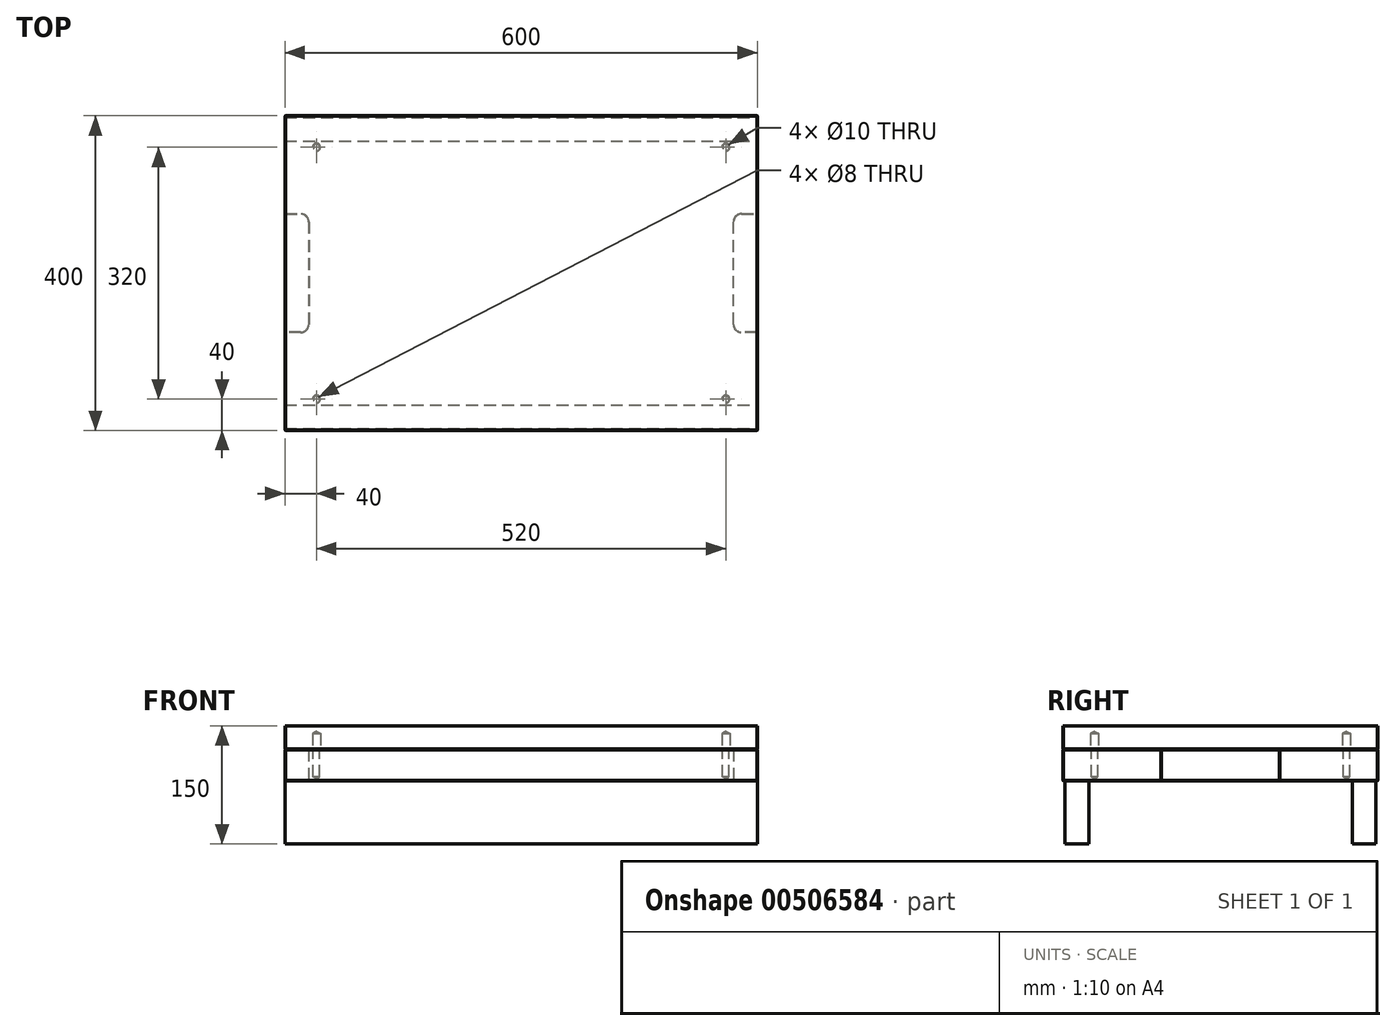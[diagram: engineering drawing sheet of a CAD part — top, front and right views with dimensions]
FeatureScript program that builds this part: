
annotation { "Feature Type Name" : "Feature", "Feature Type Description" : "" }
export const myFeature = defineFeature(function(context is Context, id is Id, definition is map)
    precondition{}
    {
        {
            assignVariable(context, id + "F0", {"name" : "Altezza_Sotto", "anyValue" : 40});
        }
        {
            assignVariable(context, id + "F1", {"name" : "Altezza_Sopra", "anyValue" : 30});
        }
        {
            var Q0;
            Q0=qCreatedBy(makeId("Top.planeOp"),FACE);
            var sketch = newSketch(context, id + "F2", { "sketchPlane" : qUnion([Q0])});
            skLineSegment(sketch, "E0", {"start": v(-250, 0) * mm, "end": v(350, 0) * mm, "construction": true});
            skLineSegment(sketch, "E1.bottom", {"start": v(350, 75) * mm, "end": v(330, 75) * mm});
            skLineSegment(sketch, "E1.top", {"start": v(350, -75) * mm, "end": v(330, -75) * mm});
            skLineSegment(sketch, "E1.left", {"start": v(350, 75) * mm, "end": v(350, -75) * mm});
            skLineSegment(sketch, "E1.right", {"start": v(320, 65) * mm, "end": v(320, -65) * mm});
            skPoint(sketch, "E2.visualSharp", {"position": v(320, -75) * mm});
            skArc(sketch, "E2.filletArc", {"start": v(320, -65) * mm, "mid": v(322.93, -72.07) * mm, "end": v(330, -75) * mm});
            skPoint(sketch, "E3.visualSharp", {"position": v(320, 75) * mm});
            skArc(sketch, "E3.filletArc", {"start": v(330, 75) * mm, "mid": v(322.93, 72.07) * mm, "end": v(320, 65) * mm});
            skLineSegment(sketch, "E4", {"start": v(50, 200) * mm, "end": v(50, -200) * mm, "construction": true});
            skLineSegment(sketch, "E5.MirrorCS", {"start": v(-250, 75) * mm, "end": v(-230, 75) * mm});
            skLineSegment(sketch, "E6.MirrorCS", {"start": v(-220, 65) * mm, "end": v(-220, -65) * mm});
            skArc(sketch, "E7.MirrorCS", {"start": v(-220, -65) * mm, "mid": v(-222.93, -72.07) * mm, "end": v(-230, -75) * mm});
            skArc(sketch, "E8.MirrorCS", {"start": v(-230, 75) * mm, "mid": v(-222.93, 72.07) * mm, "end": v(-220, 65) * mm});
            skLineSegment(sketch, "E9.MirrorCS", {"start": v(-250, -75) * mm, "end": v(-230, -75) * mm});
            skPoint(sketch, "E10", {"position": v(-210, 160) * mm});
            skPoint(sketch, "E11", {"position": v(310, 160) * mm});
            skPoint(sketch, "E12", {"position": v(310, -160) * mm});
            skPoint(sketch, "E13", {"position": v(-210, -160) * mm});
            skLineSegment(sketch, "E14", {"start": v(-220, 0) * mm, "end": v(-250, 0) * mm});
            skLineSegment(sketch, "E15.bottom", {"start": v(350, 200) * mm, "end": v(-250, 200) * mm});
            skLineSegment(sketch, "E15.top", {"start": v(350, -200) * mm, "end": v(-250, -200) * mm});
            skLineSegment(sketch, "E15.left", {"start": v(350, 200) * mm, "end": v(350, -200) * mm});
            skLineSegment(sketch, "E15.right", {"start": v(-250, 200) * mm, "end": v(-250, -200) * mm});
            skPoint(sketch, "E15.middle", {"position": v(50, 0) * mm});
            skSolve(sketch);
        }
        {
            var Q0;
            Q0=makeQuery(id+"F2.imprint","IMPRINT",FACE,{"disambiguationData":[TD([[makeQuery(id+"F2.imprint","IMPRINT",EDGE,{"derivedFrom":sQuery(id+"F2.wireOp",EDGE,"9696f999-dd8b-4db2-95aa-c8651f8d9f2f.bottom")}),1.0]])]});
            var Q1;
            {var subQ5=sQuery(id+"F2.wireOp",EDGE,"E1.bottom");Q1=makeQuery(id+"F2.imprint","IMPRINT",FACE,{"disambiguationData":[TD([[makeQuery(id+"F2.imprint","IMPRINT",EDGE,{"derivedFrom":subQ5}),-1.0]])]});}
            extrude(context, id + "F3", {"entities" : qUnion([Q0, Q1]), "depth" : (getVariable(context, 'Altezza_Sotto')) * mm});
        }
        {
            var Q0;
            Q0=makeQuery(id+"F3.opExtrude","CAP_FACE",FACE,{"disambiguationData":[OSD([sQuery(id+"F2.wireOp",EDGE,"E1.bottom"),sQuery(id+"F2.wireOp",EDGE,"E1.top"),sQuery(id+"F2.wireOp",EDGE,"E1.right"),sQuery(id+"F2.wireOp",EDGE,"E2.filletArc"),sQuery(id+"F2.wireOp",EDGE,"E3.filletArc"),sQuery(id+"F2.wireOp",EDGE,"E5.MirrorCS"),sQuery(id+"F2.wireOp",EDGE,"E6.MirrorCS"),sQuery(id+"F2.wireOp",EDGE,"E7.MirrorCS"),sQuery(id+"F2.wireOp",EDGE,"E8.MirrorCS"),sQuery(id+"F2.wireOp",EDGE,"E9.MirrorCS"),sQuery(id+"F2.wireOp",EDGE,"E15.bottom"),sQuery(id+"F2.wireOp",EDGE,"E15.top"),sQuery(id+"F2.wireOp",EDGE,"E15.left"),sQuery(id+"F2.wireOp",EDGE,"E15.right")])],"isStart":false});
            var sketch = newSketch(context, id + "F4", { "sketchPlane" : qUnion([Q0])});
            skLineSegment(sketch, "E16.bottom", {"start": v(-250, 200) * mm, "end": v(350, 200) * mm});
            skLineSegment(sketch, "E16.top", {"start": v(-250, -200) * mm, "end": v(350, -200) * mm});
            skLineSegment(sketch, "E16.left", {"start": v(-250, 200) * mm, "end": v(-250, -200) * mm});
            skLineSegment(sketch, "E16.right", {"start": v(350, 200) * mm, "end": v(350, -200) * mm});
            skLineSegment(sketch, "E17.0", {"start": v(-210, 160) * mm, "end": v(310, 160) * mm});
            skLineSegment(sketch, "E17.1", {"start": v(-210, 160) * mm, "end": v(-210, -160) * mm});
            skLineSegment(sketch, "E17.2", {"start": v(-210, -160) * mm, "end": v(310, -160) * mm});
            skLineSegment(sketch, "E17.3", {"start": v(310, 160) * mm, "end": v(310, -160) * mm});
            skSolve(sketch);
        }
        {
            var Q0;
            Q0=makeQuery(id+"F3.opExtrude","CAP_FACE",FACE,{"disambiguationData":[OSD([sQuery(id+"F2.wireOp",EDGE,"E1.bottom"),sQuery(id+"F2.wireOp",EDGE,"E1.top"),sQuery(id+"F2.wireOp",EDGE,"E1.right"),sQuery(id+"F2.wireOp",EDGE,"E2.filletArc"),sQuery(id+"F2.wireOp",EDGE,"E3.filletArc"),sQuery(id+"F2.wireOp",EDGE,"E5.MirrorCS"),sQuery(id+"F2.wireOp",EDGE,"E6.MirrorCS"),sQuery(id+"F2.wireOp",EDGE,"E7.MirrorCS"),sQuery(id+"F2.wireOp",EDGE,"E8.MirrorCS"),sQuery(id+"F2.wireOp",EDGE,"E9.MirrorCS"),sQuery(id+"F2.wireOp",EDGE,"E15.bottom"),sQuery(id+"F2.wireOp",EDGE,"E15.top"),sQuery(id+"F2.wireOp",EDGE,"E15.left"),sQuery(id+"F2.wireOp",EDGE,"E15.right")])],"isStart":true});
            var sketch = newSketch(context, id + "F5", { "sketchPlane" : qUnion([Q0])});
            skLineSegment(sketch, "E18", {"start": v(-220, 0) * mm, "end": v(320, 0) * mm, "construction": true});
            skLineSegment(sketch, "E19.bottom", {"start": v(-250, 197.5) * mm, "end": v(350, 197.5) * mm});
            skLineSegment(sketch, "E19.top", {"start": v(-250, 167.5) * mm, "end": v(350, 167.5) * mm});
            skLineSegment(sketch, "E19.left", {"start": v(-250, 197.5) * mm, "end": v(-250, 167.5) * mm});
            skLineSegment(sketch, "E19.right", {"start": v(350, 197.5) * mm, "end": v(350, 167.5) * mm});
            skLineSegment(sketch, "E20.MirrorCS", {"start": v(-250, -167.5) * mm, "end": v(350, -167.5) * mm});
            skLineSegment(sketch, "E21.MirrorCS", {"start": v(350, -197.5) * mm, "end": v(350, -167.5) * mm});
            skLineSegment(sketch, "E22.MirrorCS", {"start": v(-250, -197.5) * mm, "end": v(350, -197.5) * mm});
            skLineSegment(sketch, "E23.MirrorCS", {"start": v(-250, -197.5) * mm, "end": v(-250, -167.5) * mm});
            skSolve(sketch);
        }
        {
            var Q0;
            Q0=makeQuery(id+"F5.imprint","IMPRINT",FACE,{"disambiguationData":[TD([[makeQuery(id+"F5.imprint","IMPRINT",EDGE,{"derivedFrom":sQuery(id+"F5.wireOp",EDGE,"E19.bottom")}),-1.0]])]});
            var Q1;
            Q1=makeQuery(id+"F5.imprint","IMPRINT",FACE,{"disambiguationData":[TD([[makeQuery(id+"F5.imprint","IMPRINT",EDGE,{"derivedFrom":sQuery(id+"F5.wireOp",EDGE,"E20.MirrorCS")}),-1.0]])]});
            extrude(context, id + "F6", {"entities" : qUnion([Q0, Q1]), "depth" : 80 * mm});
        }
        {
            var Q0;
            Q0=sQuery(id+"F4.wireOp",VERTEX,"E17.1.start");
            var Q1;
            Q1=sQuery(id+"F4.wireOp",VERTEX,"E17.0.end");
            var Q2;
            Q2=sQuery(id+"F4.wireOp",VERTEX,"E17.3.end");
            var Q3;
            Q3=sQuery(id+"F4.wireOp",VERTEX,"E17.2.start");
            var Q4;
            Q4=makeQuery(id+"F3.opExtrude","SWEPT_BODY",BODY,{"disambiguationData":[OSD([sQuery(id+"F2.wireOp",EDGE,"9696f999-dd8b-4db2-95aa-c8651f8d9f2f.bottom"),sQuery(id+"F2.wireOp",EDGE,"9696f999-dd8b-4db2-95aa-c8651f8d9f2f.top"),sQuery(id+"F2.wireOp",EDGE,"9696f999-dd8b-4db2-95aa-c8651f8d9f2f.left"),sQuery(id+"F2.wireOp",EDGE,"9696f999-dd8b-4db2-95aa-c8651f8d9f2f.right"),sQuery(id+"F2.wireOp",EDGE,"E1.bottom"),sQuery(id+"F2.wireOp",EDGE,"E1.top"),sQuery(id+"F2.wireOp",EDGE,"E1.right"),sQuery(id+"F2.wireOp",EDGE,"E2.filletArc"),sQuery(id+"F2.wireOp",EDGE,"E3.filletArc"),sQuery(id+"F2.wireOp",EDGE,"E5.MirrorCS"),sQuery(id+"F2.wireOp",EDGE,"E6.MirrorCS"),sQuery(id+"F2.wireOp",EDGE,"E7.MirrorCS"),sQuery(id+"F2.wireOp",EDGE,"E8.MirrorCS"),sQuery(id+"F2.wireOp",EDGE,"E9.MirrorCS")])]});
            hole(context, id + "F7", {"style" : HoleStyle.SIMPLE, "endStyle" : HoleEndStyle.BLIND, "holeDiameter" : 8 * mm, "holeDepth" : 35 * mm, "isTappedThrough" : true, "tappedDepth" : 12 * mm, "tapClearance" : 3, "startFromSketch" : true, "locations" : qUnion([Q0, Q1, Q2, Q3]), "scope" : qUnion([Q4])});
        }
        {
            var Q0;
            {var subQ1=makeQuery(id+"F3.opExtrude","CAP_EDGE",EDGE,{"disambiguationData":[OSD([sQuery(id+"F2.wireOp",EDGE,"E1.bottom")])],"isStart":false});Q0=makeQuery(id+"F4.imprint","IMPRINT",FACE,{"disambiguationData":[TD([[makeQuery(id+"F4.imprint","IMPRINT",EDGE,{"derivedFrom":subQ1}),1.0]])]});}
            var Q1;
            {var subQ4=sQuery(id+"F4.wireOp",EDGE,"E16.bottom");Q1=makeQuery(id+"F4.imprint","IMPRINT",FACE,{"disambiguationData":[TD([[makeQuery(id+"F4.imprint","IMPRINT",EDGE,{"derivedFrom":subQ4}),1.0]])]});}
            var Q2;
            {var subQ0=makeQuery(id+"F3.opExtrude","CAP_EDGE",EDGE,{"disambiguationData":[OSD([sQuery(id+"F2.wireOp",EDGE,"E5.MirrorCS")])],"isStart":false});Q2=makeQuery(id+"F4.imprint","IMPRINT",FACE,{"disambiguationData":[TD([[makeQuery(id+"F4.imprint","IMPRINT",EDGE,{"derivedFrom":subQ0}),-1.0]])]});}
            var Q3;
            Q3=makeQuery(id+"F4.imprint","IMPRINT",FACE,{"disambiguationData":[TD([[makeQuery(id+"F4.imprint","IMPRINT",EDGE,{"derivedFrom":sQuery(id+"F4.wireOp",EDGE,"E17.0")}),-1.0]])]});
            var Q4;
            {var subQ4=sQuery(id+"F4.wireOp",EDGE,"E16.bottom");Q4=makeQuery(id+"F4.imprint","IMPRINT",FACE,{"disambiguationData":[TD([[makeQuery(id+"F4.imprint","IMPRINT",EDGE,{"derivedFrom":subQ4}),1.0]])]});}
            var Q5;
            Q5=makeQuery(id+"F4.imprint","IMPRINT",FACE,{"disambiguationData":[TD([[makeQuery(id+"F4.imprint","IMPRINT",EDGE,{"derivedFrom":sQuery(id+"F4.wireOp",EDGE,"E17.0")}),-1.0]])]});
            extrude(context, id + "F8", {"entities" : qUnion([Q0, Q1, Q2, Q3, Q4, Q5]), "depth" : (getVariable(context, 'Altezza_Sopra')) * mm});
        }
        {
            var Q0;
            Q0=makeQuery(id+"F8.opExtrude","CAP_FACE",FACE,{"disambiguationData":[OSD([sQuery(id+"F4.wireOp",EDGE,"E16.bottom"),sQuery(id+"F4.wireOp",EDGE,"E16.top"),sQuery(id+"F4.wireOp",EDGE,"E16.left"),sQuery(id+"F4.wireOp",EDGE,"E16.right")])],"isStart":false});
            var Q1;
            Q1=makeQuery(id+"F8.opExtrude","CAP_FACE",FACE,{"disambiguationData":[OSD([sQuery(id+"F4.wireOp",EDGE,"E16.bottom"),sQuery(id+"F4.wireOp",EDGE,"E16.top"),sQuery(id+"F4.wireOp",EDGE,"E16.left"),sQuery(id+"F4.wireOp",EDGE,"E16.right")])],"isStart":true});
            var Q2;
            Q2=makeQuery(id+"F8.opExtrude","SWEPT_EDGE",EDGE,{"disambiguationData":[OSD([sQuery(id+"F4.wireOp",EDGE,"E16.bottom"),sQuery(id+"F4.wireOp",EDGE,"E16.right")])]});
            var Q3;
            Q3=makeQuery(id+"F8.opExtrude","SWEPT_EDGE",EDGE,{"disambiguationData":[OSD([sQuery(id+"F4.wireOp",EDGE,"E16.bottom"),sQuery(id+"F4.wireOp",EDGE,"E16.left")])]});
            var Q4;
            Q4=makeQuery(id+"F8.opExtrude","SWEPT_EDGE",EDGE,{"disambiguationData":[OSD([sQuery(id+"F4.wireOp",EDGE,"E16.top"),sQuery(id+"F4.wireOp",EDGE,"E16.left")])]});
            var Q5;
            Q5=makeQuery(id+"F8.opExtrude","SWEPT_EDGE",EDGE,{"disambiguationData":[OSD([sQuery(id+"F4.wireOp",EDGE,"E16.top"),sQuery(id+"F4.wireOp",EDGE,"E16.right")])]});
            chamfer(context, id + "F9", {"entities" : qUnion([Q0, Q1, Q2, Q3, Q4, Q5]), "width" : 0.5 * mm, "tangentPropagation" : true});
        }
        {
            var Q0;
            Q0=sQuery(id+"F4.wireOp",VERTEX,"E17.1.start");
            var Q1;
            Q1=sQuery(id+"F4.wireOp",VERTEX,"E17.0.end");
            var Q2;
            Q2=sQuery(id+"F4.wireOp",VERTEX,"E17.3.end");
            var Q3;
            Q3=sQuery(id+"F4.wireOp",VERTEX,"E17.2.start");
            var Q4;
            Q4=makeQuery(id+"F8.opExtrude","SWEPT_BODY",BODY,{"disambiguationData":[OSD([sQuery(id+"F4.wireOp",EDGE,"E16.bottom"),sQuery(id+"F4.wireOp",EDGE,"E16.top"),sQuery(id+"F4.wireOp",EDGE,"E16.left"),sQuery(id+"F4.wireOp",EDGE,"E16.right")])]});
            hole(context, id + "F10", {"style" : HoleStyle.SIMPLE, "endStyle" : HoleEndStyle.BLIND, "oppositeDirection" : true, "holeDiameter" : 10 * mm, "holeDepth" : 20 * mm, "isTappedThrough" : true, "tappedDepth" : 12 * mm, "tapClearance" : 3, "locations" : qUnion([Q0, Q1, Q2, Q3]), "scope" : qUnion([Q4])});
        }
        {
            var Q0;
            Q0=makeQuery(id+"F3.opExtrude","CAP_FACE",FACE,{"disambiguationData":[OSD([sQuery(id+"F2.wireOp",EDGE,"E1.bottom"),sQuery(id+"F2.wireOp",EDGE,"E1.top"),sQuery(id+"F2.wireOp",EDGE,"E1.right"),sQuery(id+"F2.wireOp",EDGE,"E2.filletArc"),sQuery(id+"F2.wireOp",EDGE,"E3.filletArc"),sQuery(id+"F2.wireOp",EDGE,"E5.MirrorCS"),sQuery(id+"F2.wireOp",EDGE,"E6.MirrorCS"),sQuery(id+"F2.wireOp",EDGE,"E7.MirrorCS"),sQuery(id+"F2.wireOp",EDGE,"E8.MirrorCS"),sQuery(id+"F2.wireOp",EDGE,"E9.MirrorCS"),sQuery(id+"F2.wireOp",EDGE,"E15.bottom"),sQuery(id+"F2.wireOp",EDGE,"E15.top"),sQuery(id+"F2.wireOp",EDGE,"E15.left"),sQuery(id+"F2.wireOp",EDGE,"E15.right")])],"isStart":false});
            var Q1;
            {var subQ0=sQuery(id+"F2.wireOp",EDGE,"E15.right");var subQ1=sQuery(id+"F2.wireOp",EDGE,"E15.left");var subQ2=sQuery(id+"F2.wireOp",EDGE,"E15.top");var subQ3=sQuery(id+"F2.wireOp",EDGE,"E15.bottom");Q1=makeQuery(id+"FSn3DBmeKnvXifK_2.boolean.opBoolean","MERGE",FACE,{"derivedFrom":[makeQuery(id+"F3.opExtrude","CAP_FACE",FACE,{"disambiguationData":[OSD([sQuery(id+"F2.wireOp",EDGE,"E1.bottom"),sQuery(id+"F2.wireOp",EDGE,"E1.top"),sQuery(id+"F2.wireOp",EDGE,"E1.right"),sQuery(id+"F2.wireOp",EDGE,"E2.filletArc"),sQuery(id+"F2.wireOp",EDGE,"E3.filletArc"),sQuery(id+"F2.wireOp",EDGE,"E5.MirrorCS"),sQuery(id+"F2.wireOp",EDGE,"E6.MirrorCS"),sQuery(id+"F2.wireOp",EDGE,"E7.MirrorCS"),sQuery(id+"F2.wireOp",EDGE,"E8.MirrorCS"),sQuery(id+"F2.wireOp",EDGE,"E9.MirrorCS"),subQ3,subQ2,subQ1,subQ0])],"isStart":true}),makeQuery(id+"FSn3DBmeKnvXifK_2.opExtrude","CAP_FACE",FACE,{"disambiguationData":[OSD([subQ3,subQ2,subQ1,subQ0])],"isStart":true})]});}
            var Q2;
            Q2=makeQuery(id+"F3.opExtrude","SWEPT_FACE",FACE,{"disambiguationData":[OSD([sQuery(id+"F2.wireOp",EDGE,"E15.top")])]});
            var Q3;
            {var subQ0=sQuery(id+"F2.wireOp",EDGE,"E15.left");Q3=makeQuery(id+"FSn3DBmeKnvXifK_2.boolean.opBoolean","MERGE",FACE,{"derivedFrom":[makeQuery(id+"F3.opExtrude","SWEPT_FACE",FACE,{"disambiguationData":[OSD([subQ0]),TDD([makeQuery(id+"F2.imprint","IMPRINT",EDGE,{"disambiguationData":[TD([[makeQuery(id+"F2.imprint","INTERSECT",VERTEX,{"derivedFrom":[sQuery(id+"F2.wireOp",EDGE,"E1.bottom"),subQ0]}),1.0]])],"derivedFrom":subQ0})])]}),makeQuery(id+"F3.opExtrude","SWEPT_FACE",FACE,{"disambiguationData":[OSD([subQ0]),TDD([makeQuery(id+"F2.imprint","IMPRINT",EDGE,{"disambiguationData":[TD([[makeQuery(id+"F2.imprint","INTERSECT",VERTEX,{"derivedFrom":[sQuery(id+"F2.wireOp",EDGE,"E1.top"),subQ0]}),-1.0]])],"derivedFrom":subQ0})])]}),makeQuery(id+"FSn3DBmeKnvXifK_2.opExtrude","SWEPT_FACE",FACE,{"disambiguationData":[OSD([subQ0])]})]});}
            var Q4;
            {var subQ0=sQuery(id+"F2.wireOp",EDGE,"E15.right");Q4=makeQuery(id+"FSn3DBmeKnvXifK_2.boolean.opBoolean","MERGE",FACE,{"derivedFrom":[makeQuery(id+"F3.opExtrude","SWEPT_FACE",FACE,{"disambiguationData":[OSD([subQ0]),TDD([makeQuery(id+"F2.imprint","IMPRINT",EDGE,{"disambiguationData":[TD([[makeQuery(id+"F2.imprint","INTERSECT",VERTEX,{"derivedFrom":[sQuery(id+"F2.wireOp",EDGE,"E5.MirrorCS"),subQ0]}),1.0]])],"derivedFrom":subQ0})])]}),makeQuery(id+"F3.opExtrude","SWEPT_FACE",FACE,{"disambiguationData":[OSD([subQ0]),TDD([makeQuery(id+"F2.imprint","IMPRINT",EDGE,{"disambiguationData":[TD([[makeQuery(id+"F2.imprint","INTERSECT",VERTEX,{"derivedFrom":[sQuery(id+"F2.wireOp",EDGE,"E9.MirrorCS"),subQ0]}),-1.0]])],"derivedFrom":subQ0})])]}),makeQuery(id+"FSn3DBmeKnvXifK_2.opExtrude","SWEPT_FACE",FACE,{"disambiguationData":[OSD([subQ0])]})]});}
            var Q5;
            Q5=makeQuery(id+"F3.opExtrude","SWEPT_FACE",FACE,{"disambiguationData":[OSD([sQuery(id+"F2.wireOp",EDGE,"E15.bottom")])]});
            chamfer(context, id + "F11", {"entities" : qUnion([Q0, Q1, Q2, Q3, Q4, Q5]), "width" : 0.5 * mm, "tangentPropagation" : true});
        }
    });
